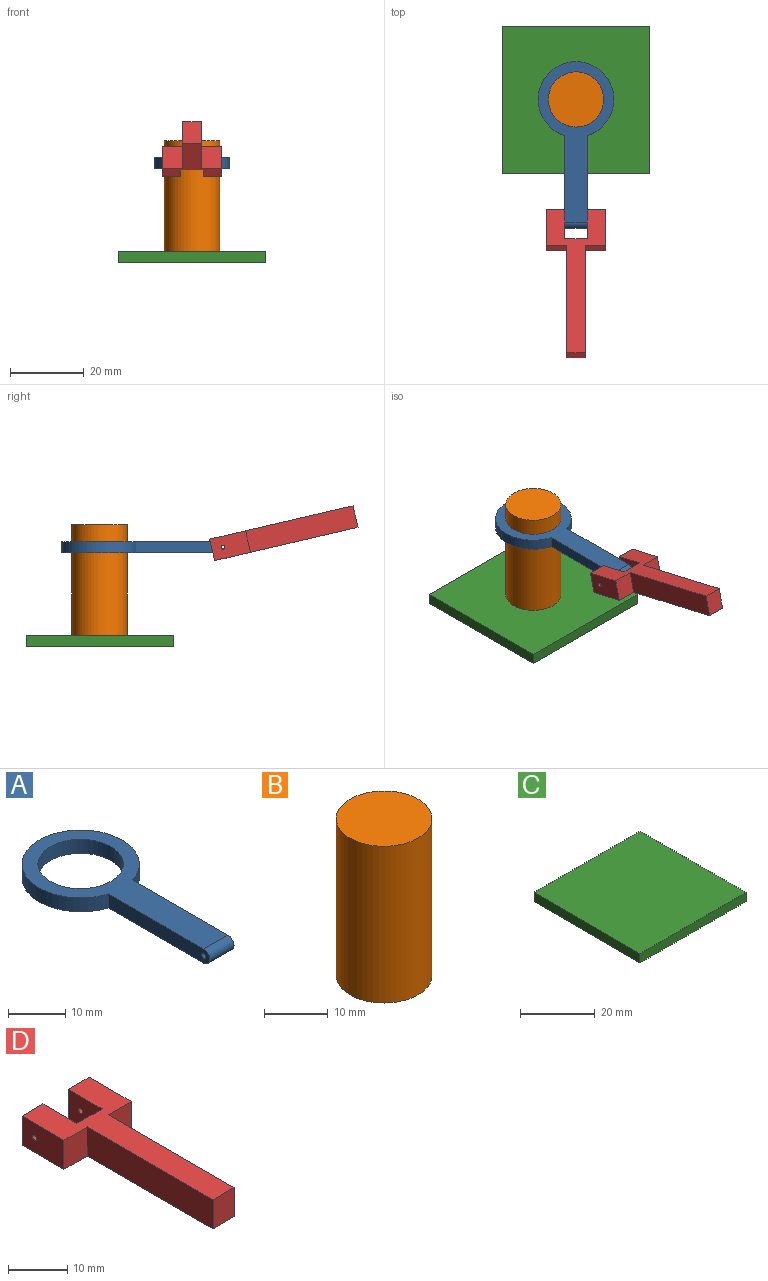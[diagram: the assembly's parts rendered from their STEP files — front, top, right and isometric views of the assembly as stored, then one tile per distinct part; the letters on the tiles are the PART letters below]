
ASSEMBLY  parts=4 mates=3
PART A: 8 faces, bbox 20.6x45.3x3 mm
  f0: cylinder r=10.29mm len=20.59mm, axis (0,0,-1), area 175.8mm2, adj f1,f3,f4,f5
  f1: plane 25.2x3mm, normal (-1,0,0), area 73.8mm2, adj f0,f4,f5,f6,f7
  f2: cylinder r=7.5mm len=15mm, axis (0,0,-1), area 141.4mm2, adj f4,f5
  f3: plane 25.2x3mm, normal (1,0,0), area 73.8mm2, adj f0,f4,f5,f6,f7
  f4: plane 43.84x20.59mm, normal (0,0,1), area 296.6mm2, adj f0,f1,f2,f3,f6
  f5: plane 43.84x20.59mm, normal (0,0,-1), area 296.6mm2, adj f0,f1,f2,f3,f6
  f6: cylinder r=1.5mm len=6mm, axis (-1,0,0), area 28.3mm2, adj f1,f3,f4,f5
  f7: cylinder r=0.5mm len=6mm, axis (-1,0,0), area 18.8mm2, adj f1,f3
PART B: 3 faces, bbox 15x15x30 mm
  f0: cylinder r=7.5mm len=30mm, axis (0,0,-1), area 1413.7mm2, adj f1,f2
  f1: plane 15x15mm, normal (0,0,1), area 176.7mm2, adj f0
  f2: plane 15x15mm, normal (0,0,-1), area 176.7mm2, adj f0
PART C: 6 faces, bbox 40x40x3 mm
  f0: plane 40x3mm, normal (0,1,0), area 120mm2, adj f1,f3,f4,f5
  f1: plane 40x3mm, normal (-1,0,0), area 120mm2, adj f0,f2,f4,f5
  f2: plane 40x3mm, normal (0,-1,0), area 120mm2, adj f1,f3,f4,f5
  f3: plane 40x3mm, normal (1,0,0), area 120mm2, adj f0,f2,f4,f5
  f4: plane 40x40mm, normal (0,0,-1), area 1600mm2, adj f0,f1,f2,f3
  f5: plane 40x40mm, normal (0,0,1), area 1600mm2, adj f0,f1,f2,f3
PART D: 16 faces, bbox 16x40x6 mm
  f0: plane 8.08x6mm, normal (1,0,0), area 47.7mm2, adj f1,f11,f12,f13,f15
  f1: plane 6x5mm, normal (0,1,0), area 30mm2, adj f0,f2,f12,f13
  f2: plane 10x6mm, normal (-1,0,0), area 59.2mm2, adj f1,f3,f12,f13,f15
  f3: plane 6x5.5mm, normal (0,-1,0), area 33mm2, adj f2,f4,f12,f13
  f4: plane 30x6mm, normal (-1,0,0), area 180mm2, adj f3,f5,f12,f13
  f5: plane 6x5mm, normal (0,-1,0), area 30mm2, adj f4,f6,f12,f13
  f6: plane 30x6mm, normal (1,0,0), area 180mm2, adj f5,f7,f12,f13
  f7: plane 6x5.5mm, normal (0,-1,0), area 33mm2, adj f6,f8,f12,f13
  f8: plane 10x6mm, normal (1,0,0), area 59.2mm2, adj f7,f9,f12,f13,f14
  f9: plane 6x5mm, normal (0,1,0), area 30mm2, adj f8,f10,f12,f13
  f10: plane 8.08x6mm, normal (-1,0,0), area 47.7mm2, adj f9,f11,f12,f13,f14
  f11: plane 6x6mm, normal (0,1,0), area 36mm2, adj f0,f10,f12,f13
  f12: plane 40x16mm, normal (0,0,1), area 261.5mm2, adj f0,f1,f2,f3,f4,f5,f6,f7
  f13: plane 40x16mm, normal (0,0,-1), area 261.5mm2, adj f0,f1,f2,f3,f4,f5,f6,f7
  f14: cylinder r=0.5mm len=5mm, axis (-1,0,0), area 15.7mm2, adj f8,f10
  f15: cylinder r=0.5mm len=5mm, axis (-1,0,0), area 15.7mm2, adj f0,f2
PLACE A t=(-24.25,14.01,-10.17)mm
PLACE B t=(-24.25,14.01,-9.03)mm
PLACE C t=(-24.25,14.01,-9.03)mm fixed
PLACE D rot(axis=(-1,0,0),13.1deg) t=(-24.25,6.99,-17.01)mm
MATE revolute A.f7 <-> D.f14  axis (-1,0,0) through (-27.25,-19.54,14.83)mm
MATE fastened C.f5 <-> B.f0  axis (0,0,1) through (-24.25,14.01,-9.03)mm
MATE slider B.f0 <-> A.f2  axis (0,0,1) through (-24.25,14.01,20.97)mm
